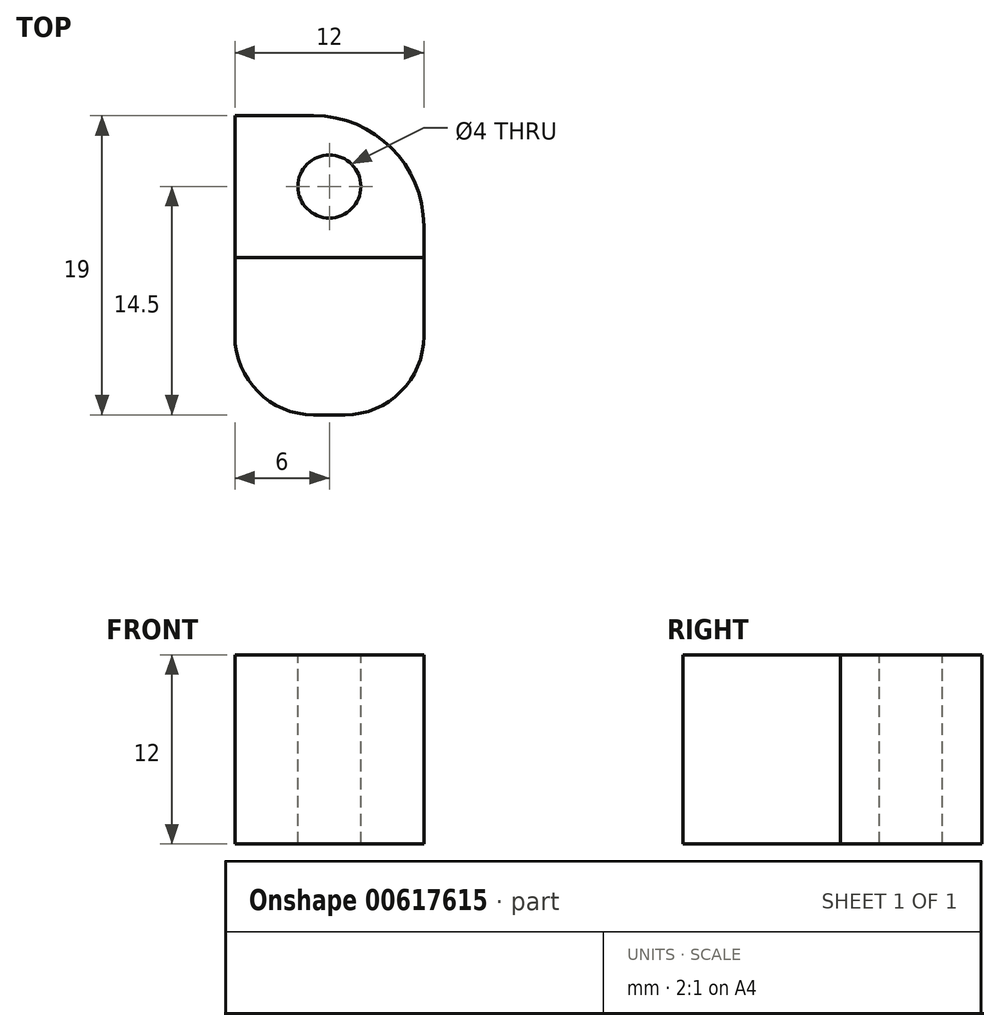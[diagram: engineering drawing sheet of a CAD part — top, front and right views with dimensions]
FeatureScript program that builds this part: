
annotation { "Feature Type Name" : "Feature", "Feature Type Description" : "" }
export const myFeature = defineFeature(function(context is Context, id is Id, definition is map)
    precondition{}
    {
        {
            var Q0;
            Q0=qCreatedBy(makeId("Front.planeOp"),FACE);
            var sketch = newSketch(context, id + "F0", { "sketchPlane" : qUnion([Q0])});
            skLineSegment(sketch, "E0.bottom", {"start": v(6, 6) * mm, "end": v(-6, 6) * mm});
            skLineSegment(sketch, "E0.top", {"start": v(6, -6) * mm, "end": v(-6, -6) * mm});
            skLineSegment(sketch, "E0.left", {"start": v(6, 6) * mm, "end": v(6, -6) * mm});
            skLineSegment(sketch, "E0.right", {"start": v(-6, 6) * mm, "end": v(-6, -6) * mm});
            skPoint(sketch, "E0.middle", {"position": v(0, 0) * mm});
            skSolve(sketch);
        }
        {
            var Q0;
            Q0=makeQuery(id+"F0.imprint","IMPRINT",FACE,{"disambiguationData":[TD([[makeQuery(id+"F0.imprint","IMPRINT",EDGE,{"derivedFrom":sQuery(id+"F0.wireOp",EDGE,"E0.bottom")}),1.0]])]});
            extrude(context, id + "F1", {"entities" : qUnion([Q0]), "depth" : 10 * mm, "offsetDistance" : 25 * mm});
        }
        {
            var Q0;
            Q0=makeQuery(id+"F1.opExtrude","CAP_FACE",FACE,{"disambiguationData":[OSD([sQuery(id+"F0.wireOp",EDGE,"E0.bottom"),sQuery(id+"F0.wireOp",EDGE,"E0.top"),sQuery(id+"F0.wireOp",EDGE,"E0.left"),sQuery(id+"F0.wireOp",EDGE,"E0.right")])],"isStart":true});
            extrude(context, id + "F2", {"entities" : qUnion([Q0]), "depth" : 9 * mm, "offsetDistance" : 25 * mm});
        }
        {
            var Q0;
            Q0=makeQuery(id+"F2.opExtrude","SWEPT_FACE",FACE,{"disambiguationData":[OSD([sQuery(id+"F0.wireOp",EDGE,"E0.bottom")])]});
            var sketch = newSketch(context, id + "F3", { "sketchPlane" : qUnion([Q0])});
            skCircle(sketch, "E1", {"center": v(0, 4.5) * mm, "radius": 2 * mm});
            skPoint(sketch, "E1.centerSnap0", {"position": v(-6, 4.5) * mm});
            skSolve(sketch);
        }
        {
            var Q0;
            Q0=makeQuery(id+"F3.imprint","IMPRINT",FACE,{"disambiguationData":[TD([[makeQuery(id+"F3.imprint","IMPRINT",EDGE,{"derivedFrom":sQuery(id+"F3.wireOp",EDGE,"E1")}),1.0]])]});
            var Q1;
            Q1=sQuery(id+"F3.wireOp",EDGE,"E1");
            extrude(context, id + "F4", {"entities" : qUnion([Q0]), "operationType" : NewBodyOperationType.REMOVE, "surfaceEntities" : qUnion([Q1]), "oppositeDirection" : true, "depth" : 13 * mm, "offsetDistance" : 25 * mm});
        }
        {
            var Q0;
            Q0=makeQuery(id+"F2.opExtrude","CAP_EDGE",EDGE,{"disambiguationData":[OSD([sQuery(id+"F0.wireOp",EDGE,"E0.left")])],"isStart":false});
            fillet(context, id + "F5", {"entities" : qUnion([Q0]), "radius" : 7 * mm, "tangentPropagation" : true, "allowEdgeOverflow" : false});
        }
        {
            var Q0;
            Q0=makeQuery(id+"F1.opExtrude","CAP_EDGE",EDGE,{"disambiguationData":[OSD([sQuery(id+"F0.wireOp",EDGE,"E0.left")])],"isStart":false});
            var Q1;
            Q1=makeQuery(id+"F1.opExtrude","CAP_EDGE",EDGE,{"disambiguationData":[OSD([sQuery(id+"F0.wireOp",EDGE,"E0.right")])],"isStart":false});
            fillet(context, id + "F6", {"entities" : qUnion([Q0, Q1]), "radius" : 5 * mm, "tangentPropagation" : true, "allowEdgeOverflow" : false});
        }
    });
